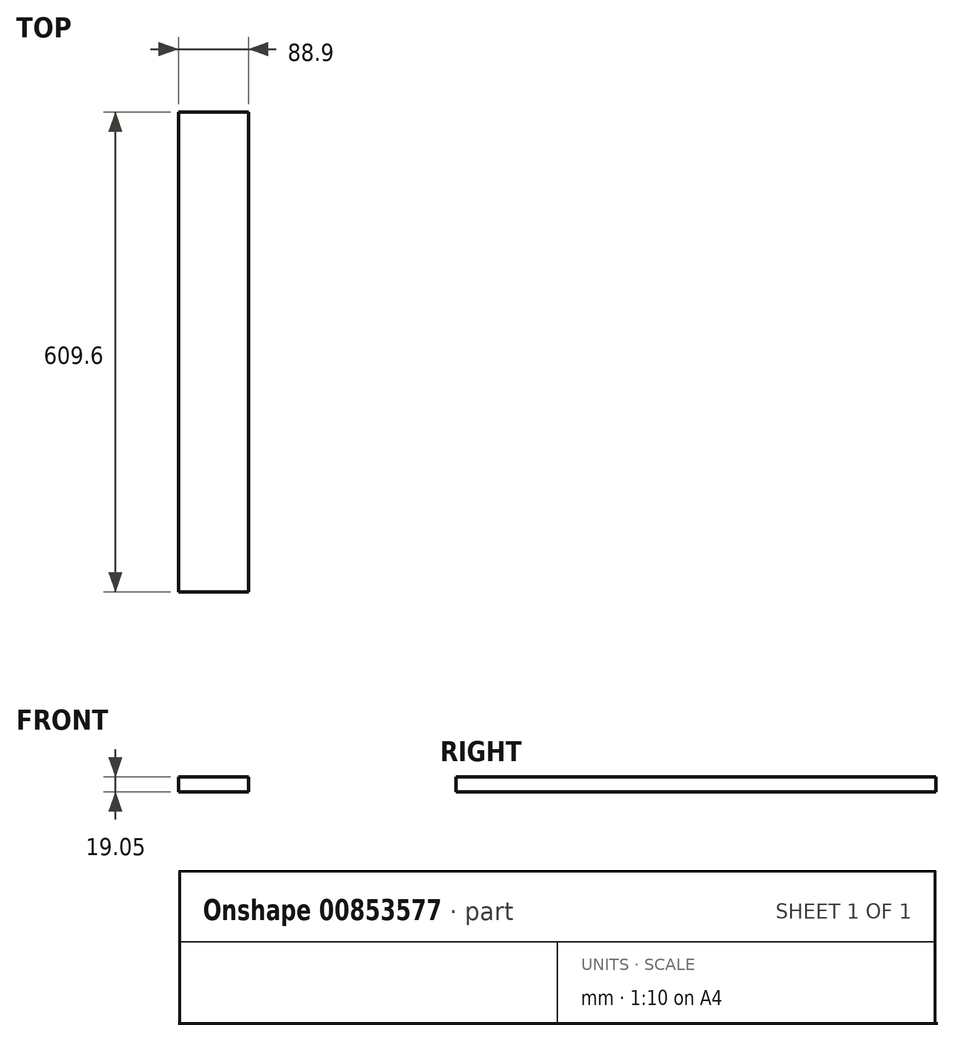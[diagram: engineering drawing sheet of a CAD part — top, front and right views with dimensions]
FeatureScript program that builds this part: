
annotation { "Feature Type Name" : "Feature", "Feature Type Description" : "" }
export const myFeature = defineFeature(function(context is Context, id is Id, definition is map)
    precondition{}
    {
        {
            var Q0;
            Q0=qCreatedBy(makeId("Front.planeOp"),FACE);
            var sketch = newSketch(context, id + "F0", { "sketchPlane" : qUnion([Q0])});
            skLineSegment(sketch, "E0.bottom", {"start": v(0, 0) * mm, "end": v(88.9, 0) * mm});
            skLineSegment(sketch, "E0.top", {"start": v(0, 19.05) * mm, "end": v(88.9, 19.05) * mm});
            skLineSegment(sketch, "E0.left", {"start": v(0, 0) * mm, "end": v(0, 19.05) * mm});
            skLineSegment(sketch, "E0.right", {"start": v(88.9, 0) * mm, "end": v(88.9, 19.05) * mm});
            skSolve(sketch);
        }
        {
            var Q0;
            Q0=makeQuery(id+"F0.imprint","IMPRINT",FACE,{"disambiguationData":[TD([[makeQuery(id+"F0.imprint","IMPRINT",EDGE,{"derivedFrom":sQuery(id+"F0.wireOp",EDGE,"E0.bottom")}),1.0]])]});
            extrude(context, id + "F1", {"entities" : qUnion([Q0]), "depth" : 609.6 * mm, "offsetDistance" : 25.4 * mm});
        }
    });
